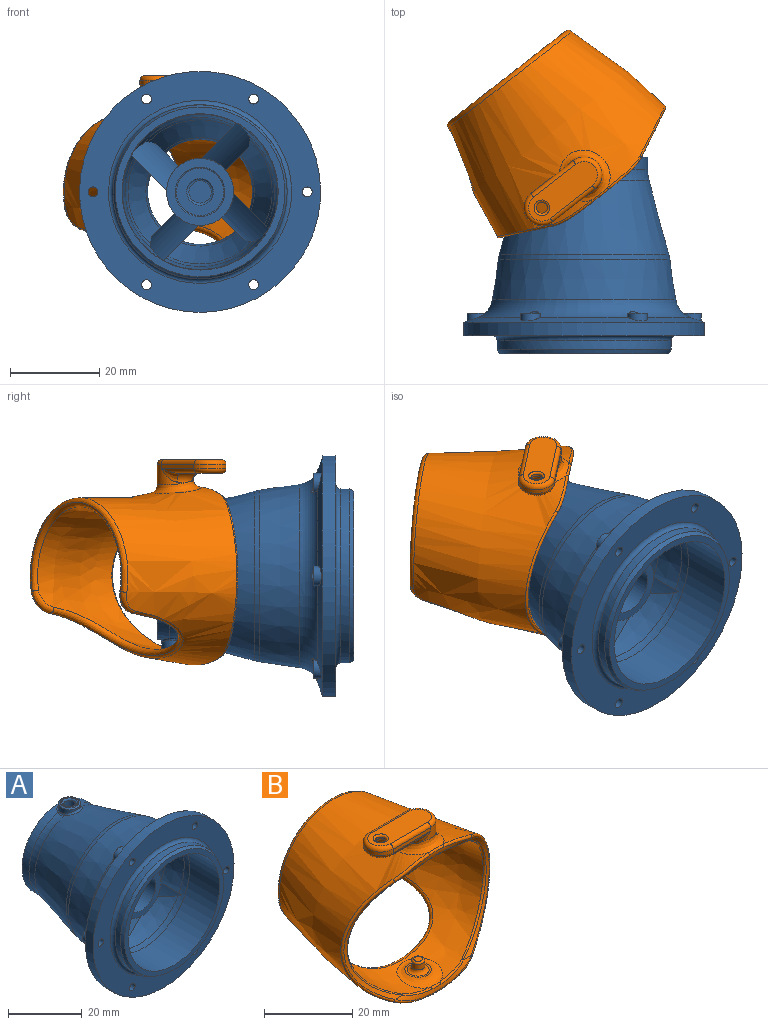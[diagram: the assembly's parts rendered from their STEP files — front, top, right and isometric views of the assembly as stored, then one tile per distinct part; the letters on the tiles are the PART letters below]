
ASSEMBLY  parts=2 mates=1
PART A: 129 faces, bbox 55.3x54.6x55.3 mm
  f0: cylinder r=7.5mm len=9.06mm, axis (0,-1,0), area 25.3mm2, adj f2,f96,f110,f113
  f1: cone r=1.75mm half-angle=16deg, axis (0,-1,0), area 93.8mm2, adj f2,f15,f107,f110,f112,f113
  f2: revolved ~10.63x5.76mm, area 59.9mm2, adj f0,f1,f110,f113
  f3: cylinder r=7.5mm len=9.06mm, axis (0,-1,0), area 25.3mm2, adj f5,f96,f102,f105
  f4: cone r=1.75mm half-angle=16deg, axis (0,-1,0), area 93.8mm2, adj f5,f29,f99,f102,f104,f105
  f5: revolved ~10.63x5.76mm, area 59.9mm2, adj f3,f4,f102,f105
  f6: cylinder r=7.5mm len=9.06mm, axis (0,-1,0), area 25.3mm2, adj f8,f96,f106,f109
  f7: cone r=1.75mm half-angle=16deg, axis (0,-1,0), area 93.8mm2, adj f8,f22,f103,f106,f108,f109
  f8: revolved ~10.63x5.76mm, area 59.9mm2, adj f6,f7,f106,f109
  f9: cone r=12.18mm half-angle=15deg, axis (0,-1,0), area 325.4mm2, adj f11,f13,f107,f110,f112,f113
  f10: cone r=16.75mm half-angle=5.7deg, axis (0,-1,0), area 172.2mm2, adj f11,f65,f110,f113
  f11: revolved ~23.49x6.22mm, area 80.8mm2, adj f9,f10,f110,f113
  f12: cylinder r=11.75mm len=15.71mm, axis (0,-1,0), area 46.2mm2, adj f13,f63,f107,f112
  f13: torus R=24.25mm, axis (0,-1,0), area 57.1mm2, adj f9,f12,f107,f112
  f14: cylinder r=1.75mm len=3.68mm, axis (0,-1,0), area 5.4mm2, adj f15,f63,f107,f112
  f15: torus R=21.75mm, axis (0,-1,0), area 10.8mm2, adj f1,f14,f107,f112
  f16: cone r=12.18mm half-angle=15deg, axis (0,-1,0), area 325.4mm2, adj f18,f20,f103,f106,f108,f109
  f17: cone r=16.75mm half-angle=5.7deg, axis (0,-1,0), area 172.2mm2, adj f18,f65,f106,f109
  f18: revolved ~23.49x6.22mm, area 80.8mm2, adj f16,f17,f106,f109
  f19: cylinder r=11.75mm len=15.71mm, axis (0,-1,0), area 46.2mm2, adj f20,f63,f103,f108
  f20: torus R=24.25mm, axis (0,-1,0), area 57.1mm2, adj f16,f19,f103,f108
  f21: cylinder r=1.75mm len=3.68mm, axis (0,-1,0), area 5.4mm2, adj f22,f63,f103,f108
  f22: torus R=21.75mm, axis (0,-1,0), area 10.8mm2, adj f7,f21,f103,f108
  f23: cone r=12.18mm half-angle=15deg, axis (0,-1,0), area 325.4mm2, adj f25,f27,f99,f102,f104,f105
  f24: cone r=16.75mm half-angle=5.7deg, axis (0,-1,0), area 172.2mm2, adj f25,f65,f102,f105
  f25: revolved ~23.49x6.22mm, area 80.8mm2, adj f23,f24,f102,f105
  f26: cylinder r=11.75mm len=15.71mm, axis (0,-1,0), area 46.2mm2, adj f27,f63,f99,f104
  f27: torus R=24.25mm, axis (0,-1,0), area 57.1mm2, adj f23,f26,f99,f104
  f28: cylinder r=1.75mm len=3.68mm, axis (0,-1,0), area 5.4mm2, adj f29,f63,f99,f104
  f29: torus R=21.75mm, axis (0,-1,0), area 10.8mm2, adj f4,f28,f99,f104
  f30: cylinder r=7.5mm len=9.06mm, axis (0,-1,0), area 25.3mm2, adj f32,f96,f101,f114
  f31: cone r=1.75mm half-angle=16deg, axis (0,-1,0), area 93.8mm2, adj f32,f98,f100,f101,f111,f114
  f32: revolved ~10.63x5.76mm, area 59.9mm2, adj f30,f31,f101,f114
  f33: cone r=12.18mm half-angle=15deg, axis (0,-1,0), area 325.4mm2, adj f36,f64,f100,f101,f111,f114
  f34: cone r=16.75mm half-angle=5.7deg, axis (0,-1,0), area 172.2mm2, adj f64,f65,f101,f114
  f35: cylinder r=11.75mm len=15.71mm, axis (0,-1,0), area 46.2mm2, adj f36,f63,f100,f111
  f36: torus R=24.25mm, axis (0,-1,0), area 57.1mm2, adj f33,f35,f100,f111
  f37: torus R=24.25mm, axis (0,-1,0), area 100.6mm2, adj f38,f39,f118,f122
  f38: cylinder r=14.25mm len=28.5mm, axis (0,-1,0), area 220.4mm2, adj f37,f40,f63,f116,f120
  f39: cone r=14.59mm half-angle=15deg, axis (0,-1,0), area 1775mm2, adj f37,f40,f73,f117,f121
  f40: torus R=24.25mm, axis (0,-1,0), area 100.6mm2, adj f38,f39,f115,f119
  f41: cylinder r=2.2mm len=4.4mm, axis (0,-1,0), area 12.5mm2, adj f42,f61,f62
  f42: plane 4.4x4.4mm, normal (0,1,0), area 11.4mm2, adj f41,f43,f44
  f43: cylinder r=1.1mm len=5mm, axis (0,1,0), area 34.6mm2, adj f42,f70
  f44: cylinder r=2.2mm len=2.15mm, axis (0,1,0), area 0.7mm2, adj f42,f62
  f45: cylinder r=2.2mm len=4.4mm, axis (0,-1,0), area 12.5mm2, adj f46,f61,f62
  f46: plane 4.4x4.4mm, normal (0,1,0), area 11.4mm2, adj f45,f47,f48
  f47: cylinder r=1.1mm len=5mm, axis (0,1,0), area 34.6mm2, adj f46,f70
  f48: cylinder r=2.2mm len=2.15mm, axis (0,1,0), area 0.7mm2, adj f46,f62
  f49: cylinder r=2.2mm len=4.4mm, axis (0,-1,0), area 12.5mm2, adj f50,f61,f62
  f50: plane 4.4x4.4mm, normal (0,1,0), area 11.4mm2, adj f49,f51,f52
  f51: cylinder r=1.1mm len=5mm, axis (0,1,0), area 34.6mm2, adj f50,f70
  f52: cylinder r=2.2mm len=2.48mm, axis (0,1,0), area 0.7mm2, adj f50,f62
  f53: cylinder r=2.2mm len=4.4mm, axis (0,-1,0), area 12.5mm2, adj f54,f61,f62
  f54: plane 4.4x4.4mm, normal (0,1,0), area 11.4mm2, adj f53,f55,f56
  f55: cylinder r=1.1mm len=5mm, axis (0,1,0), area 34.6mm2, adj f54,f70
  f56: cylinder r=2.2mm len=2.15mm, axis (0,1,0), area 0.7mm2, adj f54,f62
  f57: cylinder r=2.2mm len=4.4mm, axis (0,-1,0), area 12.5mm2, adj f58,f61,f62
  f58: plane 4.4x4.4mm, normal (0,1,0), area 11.4mm2, adj f57,f59,f60
  f59: cylinder r=1.1mm len=5mm, axis (0,1,0), area 34.6mm2, adj f58,f70
  f60: cylinder r=2.2mm len=2.15mm, axis (0,1,0), area 0.7mm2, adj f58,f62
  f61: cone r=23.92mm half-angle=71.6deg, axis (0,-1,0), area 467.7mm2, adj f41,f45,f49,f53,f57,f62,f71,f76
  f62: torus R=25.5mm, axis (0,-1,0), area 708.6mm2, adj f41,f44,f45,f48,f49,f52,f53,f56
  f63: plane 28.5x28.5mm, normal (0,1,0), area 264mm2, adj f12,f14,f19,f21,f26,f28,f35,f38
  f64: revolved ~23.49x6.22mm, area 80.8mm2, adj f33,f34,f101,f114
  f65: revolved ~34.93x34.93mm, area 218.9mm2, adj f10,f17,f24,f34,f66,f101,f102,f105
  f66: cylinder r=17.5mm len=35mm, axis (0,-1,0), area 1264.5mm2, adj f65,f67
  f67: plane 38x38mm, normal (0,-1,0), area 172mm2, adj f66,f123
  f68: cylinder r=19.5mm len=39mm, axis (0,-1,0), area 245mm2, adj f69,f123
  f69: torus R=20.5mm, axis (0,-1,0), area 196mm2, adj f68,f70
  f70: plane 54x54mm, normal (0,-1,0), area 947.2mm2, adj f43,f47,f51,f55,f59,f69,f71,f74
  f71: cylinder r=27mm len=54mm, axis (0,-1,0), area 508.9mm2, adj f61,f70
  f72: cone r=19.24mm half-angle=8.3deg, axis (0,-1,0), area 1146.2mm2, adj f62,f73
  f73: torus R=9.34mm, axis (0,-1,0), area 141.1mm2, adj f39,f72
  f74: cylinder r=1.1mm len=5mm, axis (0,1,0), area 34.6mm2, adj f70,f77
  f75: cylinder r=2.2mm len=2.48mm, axis (0,1,0), area 0.7mm2, adj f62,f77
  f76: cylinder r=2.2mm len=4.4mm, axis (0,-1,0), area 12.5mm2, adj f61,f62,f77
  f77: plane 4.4x4.4mm, normal (0,1,0), area 11.4mm2, adj f74,f75,f76
  f78: cylinder r=3mm len=6mm, axis (0,0,-1), area 25.9mm2, adj f82,f119,f120,f121,f122
  f79: plane 5x5mm, normal (0,0,1), area 5.8mm2, adj f82,f83
  f80: cone r=0mm half-angle=59deg, axis (0,0,1), area 9.4mm2, adj f81
  f81: cylinder r=1.6mm len=3.2mm, axis (0,0,1), area 25.1mm2, adj f80,f83
  f82: cone r=2.5mm half-angle=63.4deg, axis (0,0,-1), area 9.7mm2, adj f78,f79
  f83: torus R=2.1mm, axis (0,0,1), area 8.8mm2, adj f79,f81
  f84: cylinder r=3mm len=6mm, axis (0,0,1), area 25.9mm2, adj f88,f115,f116,f117,f118
  f85: plane 5x5mm, normal (0,0,-1), area 5.8mm2, adj f88,f89
  f86: cone r=0mm half-angle=59deg, axis (0,0,-1), area 9.4mm2, adj f87
  f87: cylinder r=1.6mm len=3.2mm, axis (0,0,-1), area 25.1mm2, adj f86,f89
  f88: cone r=3mm half-angle=63.4deg, axis (0,0,1), area 9.7mm2, adj f84,f85
  f89: torus R=2.1mm, axis (0,0,-1), area 8.8mm2, adj f85,f87
  f90: plane 5x5mm, normal (0,-1,0), area 19.6mm2, adj f91
  f91: torus R=2.5mm, axis (0,-1,0), area 13.9mm2, adj f90,f92
  f92: cylinder r=3mm len=6mm, axis (0,-1,0), area 28.3mm2, adj f91,f93
  f93: plane 10.6x10.6mm, normal (0,-1,0), area 60mm2, adj f92,f94
  f94: torus R=5.3mm, axis (0,-1,0), area 13.5mm2, adj f93,f95
  f95: cylinder r=5.55mm len=11.1mm, axis (0,-1,0), area 130.8mm2, adj f94,f96
  f96: plane 15x15mm, normal (0,-1,0), area 79.9mm2, adj f0,f3,f6,f30,f95
  f97: cylinder r=1.75mm len=3.68mm, axis (0,-1,0), area 5.4mm2, adj f63,f98,f100,f111
  f98: torus R=21.75mm, axis (0,-1,0), area 10.8mm2, adj f31,f97,f100,f111
  f99: plane 13.08x8.86mm, normal (-0.71,0,-0.71), area 134.8mm2, adj f4,f23,f26,f27,f28,f29,f63,f102
  f100: plane 13.08x8.86mm, normal (0.71,0,0.71), area 134.8mm2, adj f31,f33,f35,f36,f63,f97,f98,f101
  f101: cylinder r=40.28mm len=18.5mm, axis (-0.71,0,0.71), area 200mm2, adj f30,f31,f32,f33,f34,f64,f65,f100
  f102: cylinder r=32.64mm len=18.5mm, axis (-0.71,0,0.71), area 202.7mm2, adj f3,f4,f5,f23,f24,f25,f65,f99
  f103: plane 13.08x8.86mm, normal (-0.71,0,0.71), area 134.8mm2, adj f7,f16,f19,f20,f21,f22,f63,f106
  f104: plane 13.08x8.86mm, normal (0.71,0,-0.71), area 134.8mm2, adj f4,f23,f26,f27,f28,f29,f63,f105
  f105: cylinder r=40.28mm len=18.5mm, axis (0.71,0,0.71), area 200mm2, adj f3,f4,f5,f23,f24,f25,f65,f104
  f106: cylinder r=32.64mm len=18.5mm, axis (0.71,0,0.71), area 202.7mm2, adj f6,f7,f8,f16,f17,f18,f65,f103
  f107: plane 13.08x8.86mm, normal (0.71,0,0.71), area 134.8mm2, adj f1,f9,f12,f13,f14,f15,f63,f110
  f108: plane 13.08x8.86mm, normal (-0.71,0,-0.71), area 134.8mm2, adj f7,f16,f19,f20,f21,f22,f63,f109
  f109: cylinder r=40.28mm len=18.5mm, axis (0.71,0,-0.71), area 200mm2, adj f6,f7,f8,f16,f17,f18,f65,f108
  f110: cylinder r=32.64mm len=18.5mm, axis (0.71,0,-0.71), area 202.7mm2, adj f0,f1,f2,f9,f10,f11,f65,f107
  f111: plane 13.08x8.86mm, normal (0.71,0,-0.71), area 134.8mm2, adj f31,f33,f35,f36,f63,f97,f98,f114
  f112: plane 13.08x8.86mm, normal (-0.71,0,0.71), area 134.8mm2, adj f1,f9,f12,f13,f14,f15,f63,f113
  f113: cylinder r=40.28mm len=18.5mm, axis (-0.71,0,-0.71), area 200mm2, adj f0,f1,f2,f9,f10,f11,f65,f112
  f114: cylinder r=32.64mm len=18.5mm, axis (-0.71,0,-0.71), area 202.7mm2, adj f30,f31,f32,f33,f34,f64,f65,f111
  f115: bspline ~4.1x1.14mm, area 1.6mm2, adj f40,f84,f116,f117
  f116: bspline ~6.68x3mm, area 5.6mm2, adj f38,f84,f115,f118
  f117: bspline ~6.75x3.32mm, area 6.7mm2, adj f39,f84,f115,f118
  f118: bspline ~4.1x1.14mm, area 1.6mm2, adj f37,f84,f116,f117
  f119: bspline ~4.1x1.14mm, area 1.6mm2, adj f40,f78,f120,f121
  f120: bspline ~6.68x3mm, area 5.6mm2, adj f38,f78,f119,f122
  f121: bspline ~6.75x3.32mm, area 6.7mm2, adj f39,f78,f119,f122
  f122: bspline ~4.1x1.14mm, area 1.6mm2, adj f37,f78,f120,f121
  f123: cone r=19mm half-angle=26.6deg, axis (0,1,0), area 135.2mm2, adj f67,f68
  f124: plane 10.18x10.18mm, normal (0,1,0), area 4.4mm2, adj f126,f128
  f125: plane 5x5mm, normal (0,1,0), area 19.6mm2, adj f126
  f126: torus R=2.5mm, axis (0,-1,0), area 85.2mm2, adj f124,f125
  f127: cone r=1.75mm half-angle=16deg, axis (0,-1,0), area 261.9mm2, adj f128
  f128: revolved ~10.18x10.18mm, area 74.2mm2, adj f124,f127
PART B: 60 faces, bbox 52x38.4x50 mm
  f0: bspline ~47.97x39.96mm, area 2841.7mm2, adj f21,f36,f37,f38,f39,f40,f52,f55
  f1: offset ~51.97x43.96mm, area 2420.6mm2, adj f6,f11,f42,f44,f45,f46,f47,f49
  f2: plane 6x6mm, normal (0,0,-1), area 8.6mm2, adj f5,f6
  f3: cylinder r=1.5mm len=3mm, axis (0,0,1), area 14.1mm2, adj f5,f33
  f4: plane 2x2mm, normal (0,0,-1), area 3.1mm2, adj f33
  f5: torus R=2.5mm, axis (0,0,1), area 18.4mm2, adj f2,f3
  f6: bspline ~10.59x10.13mm, area 59.5mm2, adj f1,f2,f48
  f7: plane 7.34x7.34mm, normal (0,0,1), area 8.6mm2, adj f10,f11
  f8: cylinder r=1.5mm len=3mm, axis (0,0,-1), area 14.1mm2, adj f10,f32
  f9: plane 2x2mm, normal (0,0,1), area 3.1mm2, adj f32
  f10: torus R=2.5mm, axis (0,0,-1), area 18.4mm2, adj f7,f8
  f11: bspline ~10.59x10.13mm, area 59.7mm2, adj f1,f7,f43
  f12: extruded ~32.6x13.59mm, area 47.1mm2, adj f34,f35,f39,f44
  f13: extruded ~32.6x13.59mm, area 47.1mm2, adj f34,f35,f37,f47
  f14: cylinder r=4mm len=8mm, axis (0,0,1), area 61.1mm2, adj f16,f18,f21,f27,f29,f30,f31
  f15: plane 6x5.55mm, normal (0,0,-1), area 21.4mm2, adj f22,f24,f30,f59
  f16: plane 12x1mm, normal (0,1,0), area 12mm2, adj f14,f17,f24,f28
  f17: cylinder r=4mm len=8mm, axis (0,0,-1), area 12.6mm2, adj f16,f18,f23,f26
  f18: plane 12x1mm, normal (0,-1,0), area 12mm2, adj f14,f17,f22,f25
  f19: cylinder r=1.25mm len=2.5mm, axis (0,0,-1), area 3.9mm2, adj f58,f59
  f20: plane 18x6mm, normal (0,0,1), area 90.7mm2, adj f25,f26,f27,f28,f58
  f21: bspline ~11.63x11.23mm, area 83mm2, adj f0,f14,f29,f30,f41
  f22: cylinder r=1mm len=12mm, axis (1,0,0), area 14.7mm2, adj f15,f18,f23,f29,f59
  f23: torus R=3mm, axis (0,0,1), area 17mm2, adj f17,f22,f24,f59
  f24: cylinder r=1mm len=12mm, axis (-1,0,0), area 14.7mm2, adj f15,f16,f23,f31,f59
  f25: cylinder r=1mm len=12mm, axis (-1,0,0), area 18.8mm2, adj f18,f20,f26,f27
  f26: torus R=3mm, axis (0,0,1), area 17.9mm2, adj f17,f20,f25,f28
  f27: torus R=3mm, axis (0,0,1), area 17.9mm2, adj f14,f20,f25,f28
  f28: cylinder r=1mm len=12mm, axis (1,0,0), area 18.8mm2, adj f16,f20,f26,f27
  f29: bspline ~5.28x3mm, area 5mm2, adj f14,f21,f22,f30
  f30: torus R=6mm, axis (0,0,1), area 15.4mm2, adj f14,f15,f21,f29,f31
  f31: bspline ~5.28x3mm, area 4.7mm2, adj f14,f24,f30
  f32: torus R=1mm, axis (0,0,-1), area 6.5mm2, adj f8,f9
  f33: torus R=1mm, axis (0,0,1), area 6.5mm2, adj f3,f4
  f34: cylinder r=5mm len=24.38mm, axis (-1,0,0), area 28.4mm2, adj f12,f13,f36,f42,f43,f45
  f35: cylinder r=5mm len=24.38mm, axis (-1,0,0), area 25.5mm2, adj f12,f13,f38,f40,f41,f46,f48,f49
  f36: bspline ~26.71x3.99mm, area 23.8mm2, adj f0,f34,f37,f39
  f37: bspline ~36.13x13.75mm, area 41.2mm2, adj f0,f13,f36,f38
  f38: bspline ~12.46x3.98mm, area 10mm2, adj f0,f35,f37,f41
  f39: bspline ~36.13x13.75mm, area 41.2mm2, adj f0,f12,f36,f40
  f40: bspline ~11.82x3.96mm, area 10mm2, adj f0,f35,f39,f41
  f41: bspline ~5.55x0.71mm, area 3.4mm2, adj f21,f35,f38,f40
  f42: bspline ~10.91x2.51mm, area 4.9mm2, adj f1,f34,f43,f44
  f43: bspline ~3.83x0.52mm, area 1.8mm2, adj f11,f34,f42,f45
  f44: bspline ~33.56x14.96mm, area 27.8mm2, adj f1,f12,f42,f46
  f45: bspline ~11.24x2.51mm, area 4.9mm2, adj f1,f34,f43,f47
  f46: bspline ~11.24x2.51mm, area 4.9mm2, adj f1,f35,f44,f48
  f47: bspline ~33.56x14.96mm, area 27.8mm2, adj f1,f13,f45,f49
  f48: bspline ~3.83x0.52mm, area 1.8mm2, adj f6,f35,f46,f49
  f49: bspline ~10.91x2.51mm, area 4.9mm2, adj f1,f35,f47,f48
  f50: bspline ~33.07x21.76mm, area 90.5mm2, adj f1,f51,f52,f53
  f51: bspline ~5.51x4.87mm, area 12.8mm2, adj f1,f50,f54,f55
  f52: bspline ~35.07x23.09mm, area 94.2mm2, adj f0,f50,f55,f56
  f53: bspline ~6.29x5.78mm, area 12.8mm2, adj f1,f50,f54,f56
  f54: bspline ~32.33x20.32mm, area 138.1mm2, adj f1,f51,f53,f57
  f55: bspline ~6.1x4.6mm, area 8.6mm2, adj f0,f51,f52,f57
  f56: bspline ~6.11x5.37mm, area 8.6mm2, adj f0,f52,f53,f57
  f57: bspline ~33.82x20mm, area 56.1mm2, adj f0,f54,f55,f56
  f58: torus R=1.75mm, axis (0,0,1), area 7.1mm2, adj f19,f20
  f59: torus R=3.25mm, axis (0,0,1), area 37.4mm2, adj f15,f19,f22,f23,f24
PLACE A t=(0,-40,0)mm
PLACE B rot(axis=(0,0,1),37.9deg) t=(-7.37,5.47,0)mm
MATE revolute B.f3 <-> A.f78  axis (0,0,-1) through (0,-4,16.5)mm
